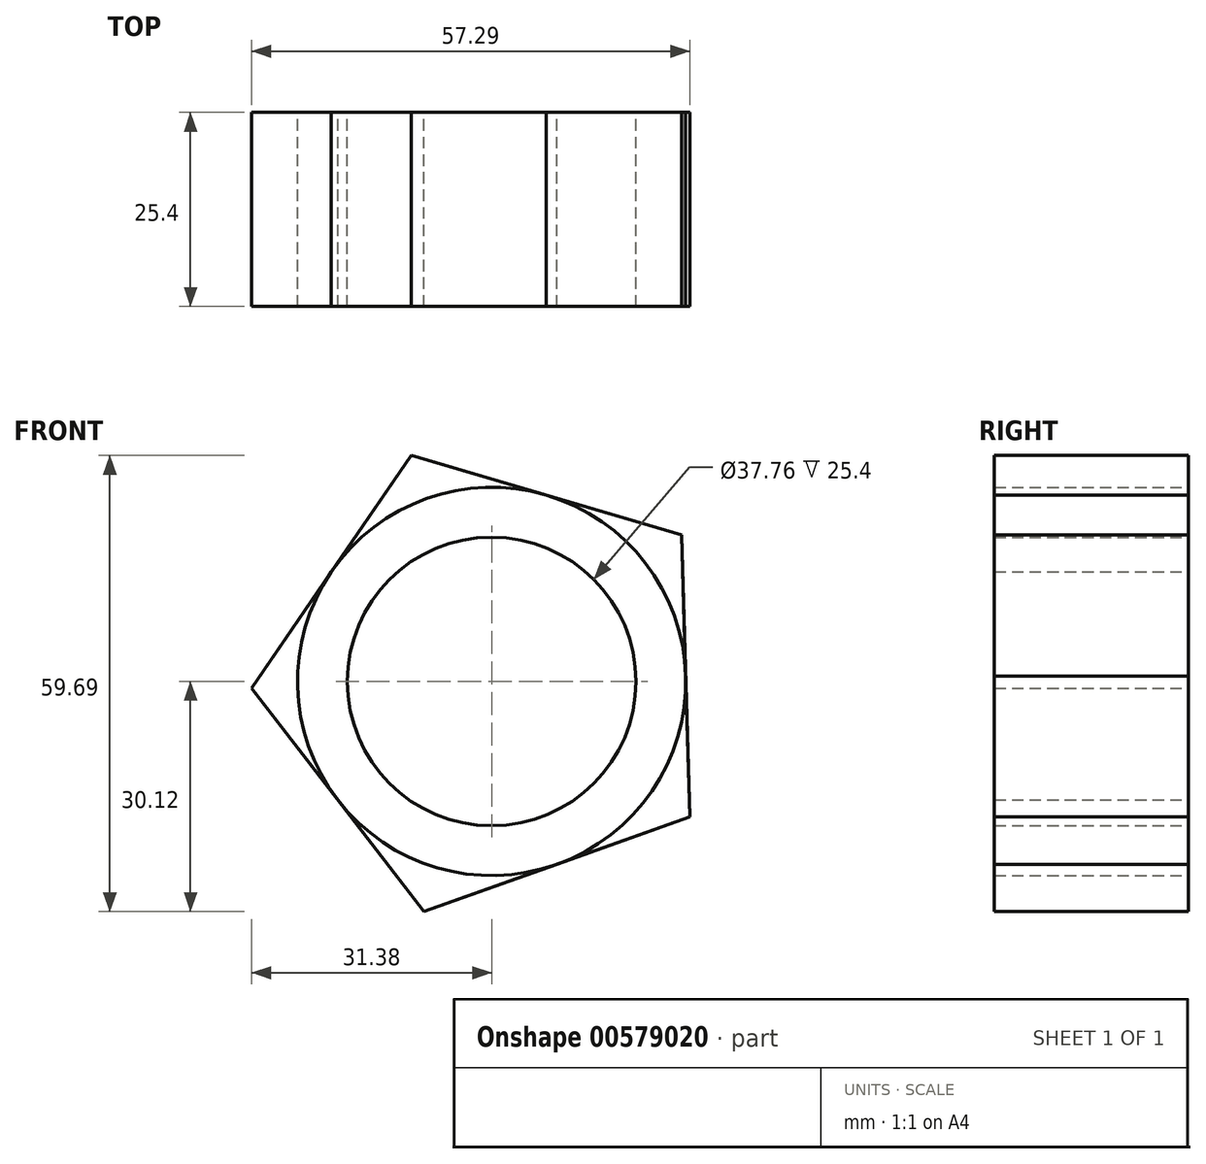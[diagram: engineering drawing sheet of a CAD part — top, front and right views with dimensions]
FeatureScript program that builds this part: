
annotation { "Feature Type Name" : "Feature", "Feature Type Description" : "" }
export const myFeature = defineFeature(function(context is Context, id is Id, definition is map)
    precondition{}
    {
        {
            var Q0;
            Q0=qCreatedBy(makeId("Front.planeOp"),FACE);
            var sketch = newSketch(context, id + "F0", { "sketchPlane" : qUnion([Q0])});
            skCircle(sketch, "E0", {"center": v(0, 0) * mm, "radius": 25.4 * mm});
            skCircle(sketch, "E1.cCircle", {"center": v(0, 0) * mm, "radius": 25.4 * mm, "construction": true});
            skLineSegment(sketch, "E1.0", {"start": v(-31.38, -0.9) * mm, "end": v(-10.54, 29.57) * mm});
            skLineSegment(sketch, "E1.1", {"start": v(-10.54, 29.57) * mm, "end": v(24.87, 19.17) * mm});
            skLineSegment(sketch, "E1.2", {"start": v(24.87, 19.17) * mm, "end": v(25.91, -17.73) * mm});
            skLineSegment(sketch, "E1.3", {"start": v(25.91, -17.73) * mm, "end": v(-8.85, -30.12) * mm});
            skLineSegment(sketch, "E1.4", {"start": v(-8.85, -30.12) * mm, "end": v(-31.38, -0.9) * mm});
            skPoint(sketch, "E1.0.midPoint", {"position": v(-20.96, 14.34) * mm});
            skCircle(sketch, "E2", {"center": v(0, 0) * mm, "radius": 18.88 * mm});
            skSolve(sketch);
        }
        {
            var Q0;
            {var subQ0=sQuery(id+"F0.wireOp",EDGE,"E1.1");var subQ1=sQuery(id+"F0.wireOp",EDGE,"E0");var subQ2=makeQuery(id+"F0.imprint","INTERSECT",VERTEX,{"derivedFrom":[subQ1,subQ0]});Q0=makeQuery(id+"F0.imprint","IMPRINT",FACE,{"disambiguationData":[TD([[makeQuery(id+"F0.imprint","IMPRINT",EDGE,{"disambiguationData":[TD([[subQ2,1.0]])],"derivedFrom":subQ1}),-1.0]])]});}
            var Q1;
            {var subQ0=sQuery(id+"F0.wireOp",EDGE,"E1.1");var subQ1=sQuery(id+"F0.wireOp",EDGE,"E0");var subQ2=makeQuery(id+"F0.imprint","INTERSECT",VERTEX,{"derivedFrom":[subQ1,subQ0]});Q1=makeQuery(id+"F0.imprint","IMPRINT",FACE,{"disambiguationData":[TD([[makeQuery(id+"F0.imprint","IMPRINT",EDGE,{"disambiguationData":[TD([[subQ2,-1.0]])],"derivedFrom":subQ1}),-1.0]])]});}
            var Q2;
            {var subQ0=sQuery(id+"F0.wireOp",EDGE,"E1.0");var subQ1=sQuery(id+"F0.wireOp",EDGE,"E0");var subQ2=makeQuery(id+"F0.imprint","INTERSECT",VERTEX,{"derivedFrom":[subQ1,subQ0]});Q2=makeQuery(id+"F0.imprint","IMPRINT",FACE,{"disambiguationData":[TD([[makeQuery(id+"F0.imprint","IMPRINT",EDGE,{"disambiguationData":[TD([[subQ2,-1.0]])],"derivedFrom":subQ1}),-1.0]])]});}
            var Q3;
            {var subQ0=sQuery(id+"F0.wireOp",EDGE,"E1.4");var subQ1=sQuery(id+"F0.wireOp",EDGE,"E0");var subQ2=makeQuery(id+"F0.imprint","INTERSECT",VERTEX,{"derivedFrom":[subQ1,subQ0]});Q3=makeQuery(id+"F0.imprint","IMPRINT",FACE,{"disambiguationData":[TD([[makeQuery(id+"F0.imprint","IMPRINT",EDGE,{"disambiguationData":[TD([[subQ2,-1.0]])],"derivedFrom":subQ1}),-1.0]])]});}
            var Q4;
            {var subQ0=sQuery(id+"F0.wireOp",EDGE,"E1.2");var subQ1=sQuery(id+"F0.wireOp",EDGE,"E0");var subQ2=makeQuery(id+"F0.imprint","INTERSECT",VERTEX,{"derivedFrom":[subQ1,subQ0]});Q4=makeQuery(id+"F0.imprint","IMPRINT",FACE,{"disambiguationData":[TD([[makeQuery(id+"F0.imprint","IMPRINT",EDGE,{"disambiguationData":[TD([[subQ2,1.0]])],"derivedFrom":subQ1}),-1.0]])]});}
            extrude(context, id + "F1", {"entities" : qUnion([Q0, Q1, Q2, Q3, Q4]), "depth" : 25.4 * mm, "offsetDistance" : 25.4 * mm});
        }
        {
            var Q0;
            Q0 = qSketchRegion(id + "F0", true);
            extrude(context, id + "F2", {"entities" : qUnion([Q0]), "depth" : 25.4 * mm, "offsetDistance" : 25.4 * mm});
        }
    });
